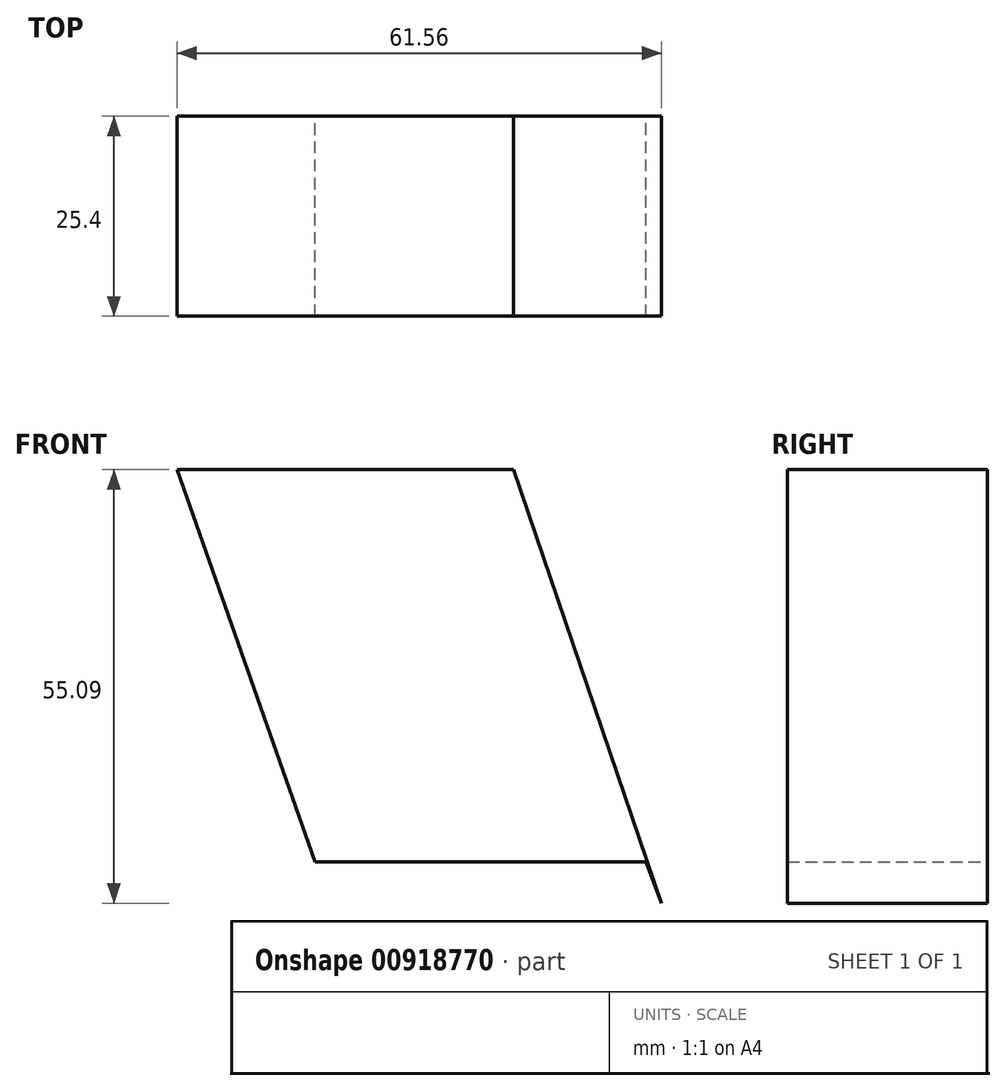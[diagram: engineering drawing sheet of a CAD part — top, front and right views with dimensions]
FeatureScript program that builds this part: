
annotation { "Feature Type Name" : "Feature", "Feature Type Description" : "" }
export const myFeature = defineFeature(function(context is Context, id is Id, definition is map)
    precondition{}
    {
        {
            var Q0;
            Q0=qCreatedBy(makeId("Front.planeOp"),FACE);
            var sketch = newSketch(context, id + "F0", { "sketchPlane" : qUnion([Q0])});
            skLineSegment(sketch, "E0", {"start": v(-30.68, 14.6) * mm, "end": v(-73.42, 14.6) * mm});
            skLineSegment(sketch, "E1", {"start": v(-73.42, 14.6) * mm, "end": v(-55.86, -35.25) * mm});
            skLineSegment(sketch, "E2", {"start": v(-55.86, -35.25) * mm, "end": v(-13.86, -35.25) * mm});
            skLineSegment(sketch, "E3", {"start": v(-13.86, -35.25) * mm, "end": v(-11.86, -40.5) * mm});
            skLineSegment(sketch, "E4", {"start": v(-11.86, -40.5) * mm, "end": v(-30.68, 14.6) * mm});
            skSolve(sketch);
        }
        {
            var Q0;
            Q0 = qSketchRegion(id + "F0", true);
            extrude(context, id + "F1", {"entities" : qUnion([Q0]), "depth" : 25.4 * mm, "offsetDistance" : 25.4 * mm});
        }
    });
